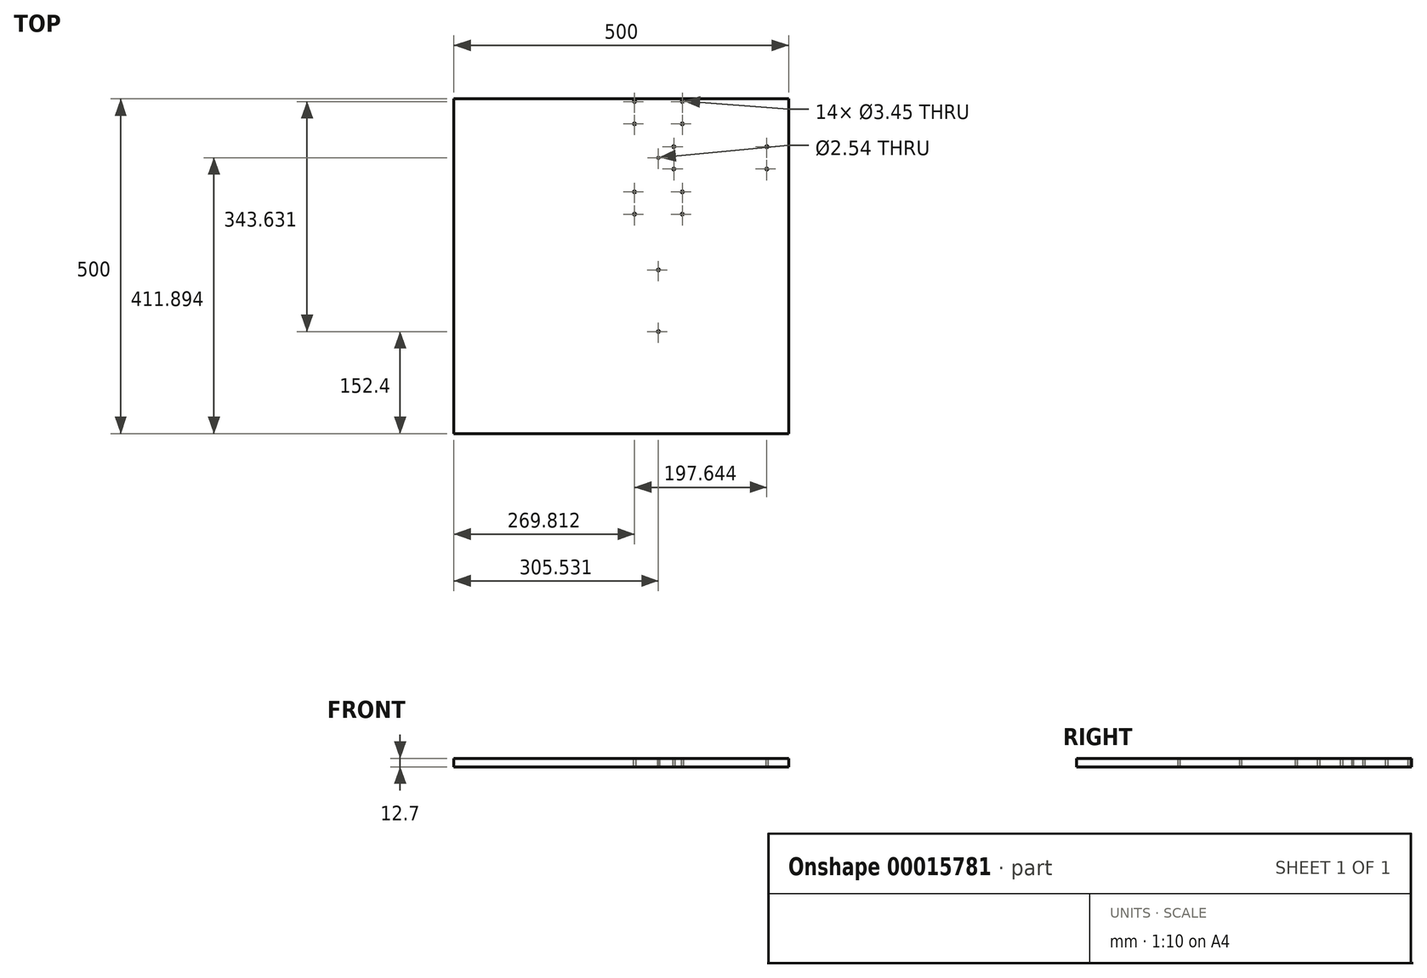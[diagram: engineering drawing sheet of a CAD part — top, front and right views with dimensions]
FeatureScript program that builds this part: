
annotation { "Feature Type Name" : "Feature", "Feature Type Description" : "" }
export const myFeature = defineFeature(function(context is Context, id is Id, definition is map)
    precondition{}
    {
        {
            var Q0;
            Q0=qCreatedBy(makeId("Top.planeOp"),FACE);
            var sketch = newSketch(context, id + "F0", { "sketchPlane" : qUnion([Q0])});
            skLineSegment(sketch, "E0.bottom", {"start": v(0, 0) * mm, "end": v(500, 0) * mm});
            skLineSegment(sketch, "E0.top", {"start": v(0, -500) * mm, "end": v(500, -500) * mm});
            skLineSegment(sketch, "E0.left", {"start": v(0, 0) * mm, "end": v(0, -500) * mm});
            skLineSegment(sketch, "E0.right", {"start": v(500, 0) * mm, "end": v(500, -500) * mm});
            skLineSegment(sketch, "E1", {"start": v(500, -88.1) * mm, "end": v(467.46, -88.1) * mm, "construction": true});
            skLineSegment(sketch, "E2", {"start": v(467.46, -88.1) * mm, "end": v(328.55, -88.1) * mm, "construction": true});
            skLineSegment(sketch, "E3", {"start": v(328.55, -104.77) * mm, "end": v(328.55, -71.44) * mm, "construction": true});
            skLineSegment(sketch, "E4", {"start": v(467.46, -104.77) * mm, "end": v(467.46, -71.44) * mm, "construction": true});
            skCircle(sketch, "E5", {"center": v(328.55, -71.44) * mm, "radius": 1.73 * mm});
            skCircle(sketch, "E6", {"center": v(328.55, -104.77) * mm, "radius": 1.73 * mm});
            skCircle(sketch, "E7", {"center": v(467.46, -104.77) * mm, "radius": 1.73 * mm});
            skCircle(sketch, "E8", {"center": v(467.46, -71.44) * mm, "radius": 1.73 * mm});
            skLineSegment(sketch, "E9", {"start": v(328.55, -88.1) * mm, "end": v(305.53, -88.1) * mm, "construction": true});
            skLineSegment(sketch, "E10", {"start": v(305.53, -155.58) * mm, "end": v(305.53, -20.64) * mm, "construction": true});
            skLineSegment(sketch, "E11", {"start": v(269.81, -20.64) * mm, "end": v(341.25, -20.64) * mm, "construction": true});
            skLineSegment(sketch, "E12", {"start": v(341.25, -37.3) * mm, "end": v(341.25, -3.97) * mm, "construction": true});
            skLineSegment(sketch, "E13", {"start": v(269.81, -37.3) * mm, "end": v(269.81, -3.97) * mm, "construction": true});
            skLineSegment(sketch, "E14", {"start": v(341.25, -3.97) * mm, "end": v(341.25, 0) * mm, "construction": true});
            skCircle(sketch, "E15", {"center": v(269.81, -3.97) * mm, "radius": 1.73 * mm});
            skCircle(sketch, "E16", {"center": v(269.81, -37.3) * mm, "radius": 1.73 * mm});
            skCircle(sketch, "E17", {"center": v(341.25, -37.3) * mm, "radius": 1.73 * mm});
            skCircle(sketch, "E18", {"center": v(341.25, -3.97) * mm, "radius": 1.73 * mm});
            skLineSegment(sketch, "E19", {"start": v(269.81, -155.58) * mm, "end": v(341.25, -155.58) * mm, "construction": true});
            skLineSegment(sketch, "E20", {"start": v(341.25, -172.24) * mm, "end": v(341.25, -138.9) * mm, "construction": true});
            skLineSegment(sketch, "E21", {"start": v(269.81, -172.24) * mm, "end": v(269.81, -138.9) * mm, "construction": true});
            skCircle(sketch, "E22", {"center": v(305.53, -88.1) * mm, "radius": 1.27 * mm});
            skLineSegment(sketch, "E23", {"start": v(328.55, -71.44) * mm, "end": v(328.55, -54.37) * mm, "construction": true});
            skLineSegment(sketch, "E24", {"start": v(328.55, -54.37) * mm, "end": v(341.25, -54.37) * mm, "construction": true});
            skLineSegment(sketch, "E25", {"start": v(341.25, -54.37) * mm, "end": v(341.25, -37.3) * mm, "construction": true});
            skCircle(sketch, "E26", {"center": v(269.81, -138.9) * mm, "radius": 1.73 * mm});
            skCircle(sketch, "E27", {"center": v(341.25, -138.9) * mm, "radius": 1.73 * mm});
            skCircle(sketch, "E28", {"center": v(341.25, -172.24) * mm, "radius": 1.73 * mm});
            skCircle(sketch, "E29", {"center": v(269.81, -172.24) * mm, "radius": 1.73 * mm});
            skLineSegment(sketch, "E30", {"start": v(305.53, -500) * mm, "end": v(305.53, -347.6) * mm, "construction": true});
            skLineSegment(sketch, "E31", {"start": v(305.53, -347.6) * mm, "end": v(305.53, -255.52) * mm, "construction": true});
            skCircle(sketch, "E32", {"center": v(305.53, -255.52) * mm, "radius": 1.73 * mm});
            skCircle(sketch, "E33", {"center": v(305.53, -347.6) * mm, "radius": 1.73 * mm});
            skLineSegment(sketch, "E34", {"start": v(305.53, -255.52) * mm, "end": v(305.53, -213.88) * mm, "construction": true});
            skLineSegment(sketch, "E35", {"start": v(269.81, -213.88) * mm, "end": v(305.53, -213.88) * mm, "construction": true});
            skLineSegment(sketch, "E36", {"start": v(269.81, -213.88) * mm, "end": v(269.81, -172.24) * mm, "construction": true});
            skSolve(sketch);
        }
        {
            var Q0;
            Q0 = qSketchRegion(id + "F0", true);
            extrude(context, id + "F1", {"entities" : qUnion([Q0]), "depth" : 12.7 * mm});
        }
    });
